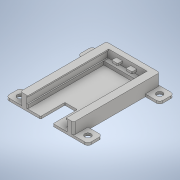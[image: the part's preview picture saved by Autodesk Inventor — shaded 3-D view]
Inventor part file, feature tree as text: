
AUTODESK INVENTOR PART (.ipt)
format: ipt  version: 2020 (Build 240168000, 168)  size: 291,840 bytes
history: native  units: in
note: dims shown in document units (in); Inventor stores cm internally (conversion verified against a paired STEP export)
features: extrude x7, sketch x7, fillet x5
ambient origin geometry x8: Origin, YZ Plane, XZ Plane, XY Plane, X Axis, Y Axis, Z Axis, Center Point
bodies: Solid1 (feature_tree)
feature tree (19):
  extrude  "Base"  Depth=0.35in
  fillet  "Fillet1"  Radius=1.4014in
  extrude  "bottom"  Depth=0.35in
  extrude  "Extrusion3"  Depth=0.35in
  extrude  "Extrusion4"  Depth=0.15in
  extrude  "Extrusion5"  Depth=0.175in
  extrude  "Extrusion6"  Depth=0.15in
  extrude  "Extrusion7"  Depth=0.15in
  fillet  "Fillet2"  Radius=0.175in
  fillet  "Fillet3"  Radius=0.175in
  fillet  "Fillet4"  Radius=0.15in
  fillet  "Fillet5"  Radius=0.175in
  sketch  "Sketch1"  dims[d0=0.35in d1=0.35in d2=1.4014in]
  sketch  "Sketch3"  dims[d3=0.35in d4=0.35in]
  sketch  "Sketch4"  dims[d5=1.65in d6=0.35in]
  sketch  "Sketch5"  dims[d7=0.35in d8=0.15in]
  sketch  "Sketch6"  dims[d9=0.175in d10=0.175in]
  sketch  "Sketch7"  dims[d11=0.15in d12=0.175in]
  sketch  "Sketch8"  dims[d13=0.175in d14=0.15in d15=0.175in d16=0.175in d17=0.15in d18=0.175in d19=0.175in d20=0.0591in d21=0.0in d22=0.0787in d23=0.1801in d24=0.125in d25=0.1801in d26=0.085in d27=0.0in d28=0.15in d29=0.15in d30=0.125in d31=0.1634in d32=0.0in d33=0.0315in d34=0.0315in d35=0.0295in d36=0.0in d37=0.3051in d38=0.3159in d39=0.5906in d40=0.0787in d41=0.0in d42=0.1181in d43=0.0787in d44=0.0in d45=0.065in d46=0.065in d47=0.2in d48=0.15in d49=0.15in d50=0.0492in d51=0.0492in d52=0.22in d53=0.15in d54=0.0in d55=0.0197in d56=0.0197in d57=0.0197in d58=0.0394in]
